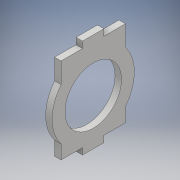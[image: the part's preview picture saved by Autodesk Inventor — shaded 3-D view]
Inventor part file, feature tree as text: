
AUTODESK INVENTOR PART (.ipt)
format: ipt  version: 2018 (Build 220112000, 112)  size: 138,240 bytes
history: native  units: mm
features: extrude x2, sketch x2, other x1
ambient origin geometry x8: Origin, YZ Plane, XZ Plane, XY Plane, X Axis, Y Axis, Z Axis, Center Point
bodies: Body1 (feature_tree)
feature tree (5):
  other  "Sólido1"
  extrude  "Extrusión1"  Depth=10.0mm
  extrude  "Extrusión2"  Depth=3.0mm TaperAngle=0.0deg
  sketch  "Boceto1"  dims[d1=10.0mm d2=10.0mm]
  sketch  "Boceto2"  dims[d3=10.0mm d9=3.0mm d10=0.0mm d11=3.0mm d12=3.0mm d13=0.0mm]
